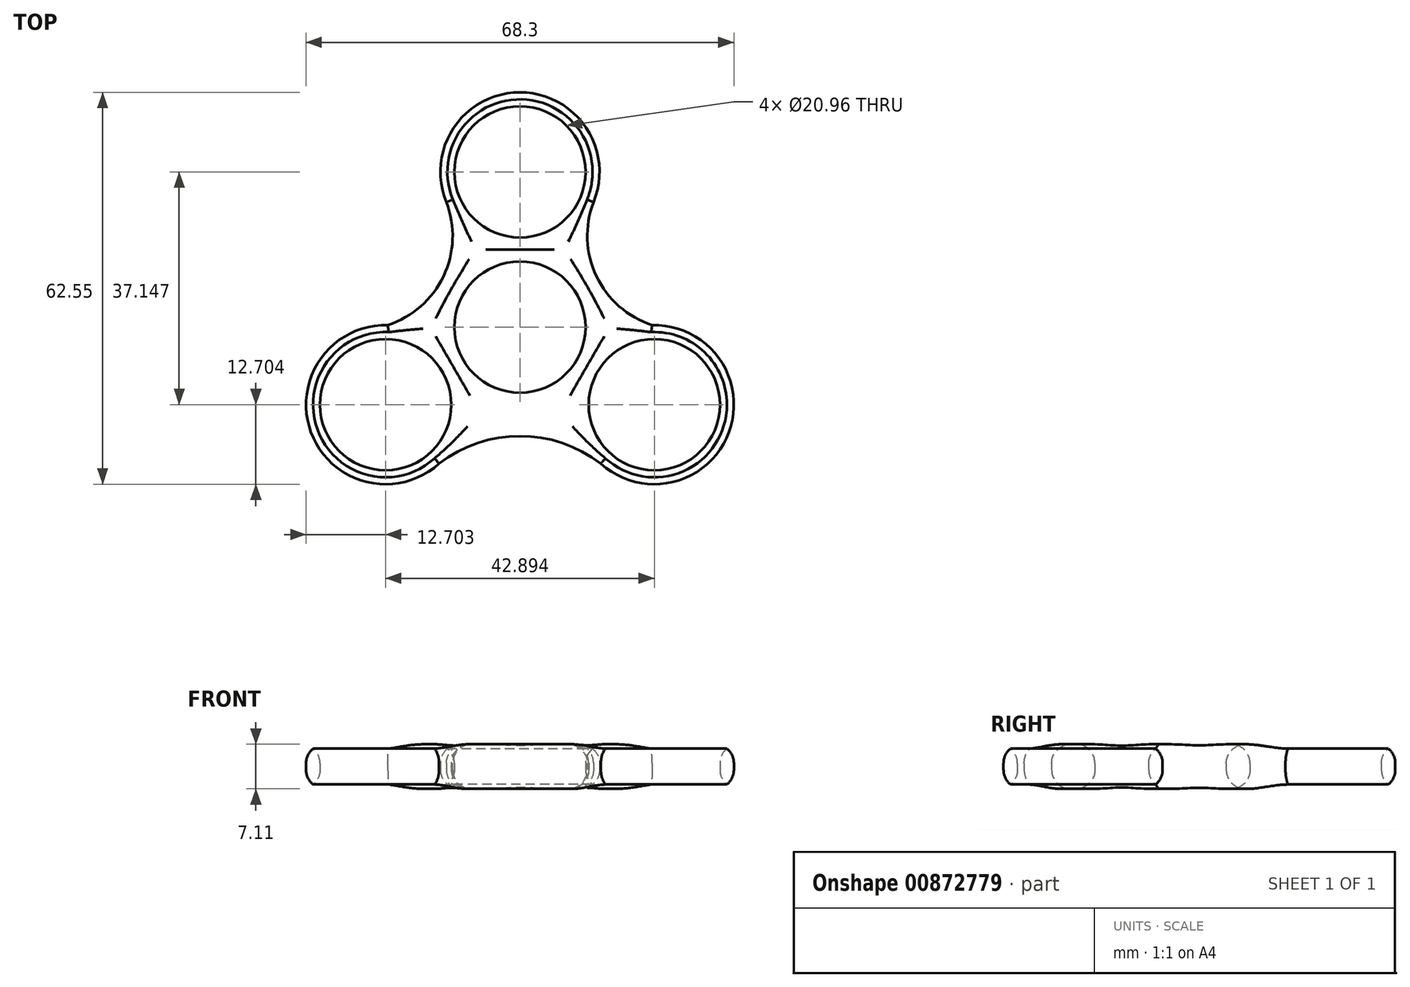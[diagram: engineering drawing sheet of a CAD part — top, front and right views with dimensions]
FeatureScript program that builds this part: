
annotation { "Feature Type Name" : "Feature", "Feature Type Description" : "" }
export const myFeature = defineFeature(function(context is Context, id is Id, definition is map)
    precondition{}
    {
        {
            var Q0;
            Q0=qCreatedBy(makeId("Top.planeOp"),FACE);
            var sketch = newSketch(context, id + "F0", { "sketchPlane" : qUnion([Q0])});
            skCircle(sketch, "E0", {"center": v(0, 47.37) * mm, "radius": 10.48 * mm});
            skCircle(sketch, "E1.1.0", {"center": v(-21.45, 10.22) * mm, "radius": 10.48 * mm});
            skCircle(sketch, "E1.2.0", {"center": v(21.45, 10.22) * mm, "radius": 10.48 * mm});
            skPoint(sketch, "E1.center", {"position": v(0, 22.6) * mm});
            skCircle(sketch, "E2", {"center": v(0, 22.6) * mm, "radius": 10.48 * mm});
            skArc(sketch, "E3", {"start": v(11.74, 42.54) * mm, "mid": v(0, 60.07) * mm, "end": v(-11.74, 42.54) * mm});
            skArc(sketch, "E4", {"start": v(12.91, 0.82) * mm, "mid": v(33.36, 5.81) * mm, "end": v(21.1, 22.92) * mm});
            skArc(sketch, "E5", {"start": v(-21.1, 22.92) * mm, "mid": v(-33.36, 5.81) * mm, "end": v(-12.91, 0.82) * mm});
            skArc(sketch, "E6", {"start": v(-21.1, 22.92) * mm, "mid": v(-12.2, 30.72) * mm, "end": v(-11.74, 42.54) * mm});
            skArc(sketch, "E7.MirrorCS", {"start": v(21.1, 22.92) * mm, "mid": v(12.2, 30.72) * mm, "end": v(11.74, 42.54) * mm});
            skArc(sketch, "E8", {"start": v(12.91, 0.82) * mm, "mid": v(0, 5.2) * mm, "end": v(-12.91, 0.82) * mm});
            skPoint(sketch, "E9.orphan", {"position": v(-13.91, 0) * mm});
            skPoint(sketch, "E10.orphan", {"position": v(13.91, 0) * mm});
            skSolve(sketch);
        }
        {
            var Q0;
            Q0=makeQuery(id+"F0.imprint","IMPRINT",FACE,{"disambiguationData":[TD([[makeQuery(id+"F0.imprint","IMPRINT",EDGE,{"derivedFrom":sQuery(id+"F0.wireOp",EDGE,"E0")}),-1.0]])]});
            extrude(context, id + "F1", {"entities" : qUnion([Q0]), "depth" : 7.11 * mm, "offsetDistance" : 25.4 * mm});
        }
        {
            var Q0;
            Q0=makeQuery(id+"F1.opExtrude","CAP_FACE",FACE,{"disambiguationData":[OSD([sQuery(id+"F0.wireOp",EDGE,"E0"),sQuery(id+"F0.wireOp",EDGE,"E1.1.0"),sQuery(id+"F0.wireOp",EDGE,"E1.2.0"),sQuery(id+"F0.wireOp",EDGE,"E2"),sQuery(id+"F0.wireOp",EDGE,"E3"),sQuery(id+"F0.wireOp",EDGE,"E4"),sQuery(id+"F0.wireOp",EDGE,"E5"),sQuery(id+"F0.wireOp",EDGE,"E6"),sQuery(id+"F0.wireOp",EDGE,"E7.MirrorCS"),sQuery(id+"F0.wireOp",EDGE,"E8")])],"isStart":false});
            var Q1;
            Q1=makeQuery(id+"F1.opExtrude","CAP_FACE",FACE,{"disambiguationData":[OSD([sQuery(id+"F0.wireOp",EDGE,"E0"),sQuery(id+"F0.wireOp",EDGE,"E1.1.0"),sQuery(id+"F0.wireOp",EDGE,"E1.2.0"),sQuery(id+"F0.wireOp",EDGE,"E2"),sQuery(id+"F0.wireOp",EDGE,"E3"),sQuery(id+"F0.wireOp",EDGE,"E4"),sQuery(id+"F0.wireOp",EDGE,"E5"),sQuery(id+"F0.wireOp",EDGE,"E6"),sQuery(id+"F0.wireOp",EDGE,"E7.MirrorCS"),sQuery(id+"F0.wireOp",EDGE,"E8")])],"isStart":true});
            fillet(context, id + "F2", {"entities" : qUnion([Q0, Q1]), "radius" : 3.05 * mm, "tangentPropagation" : true, "allowEdgeOverflow" : false});
        }
    });
